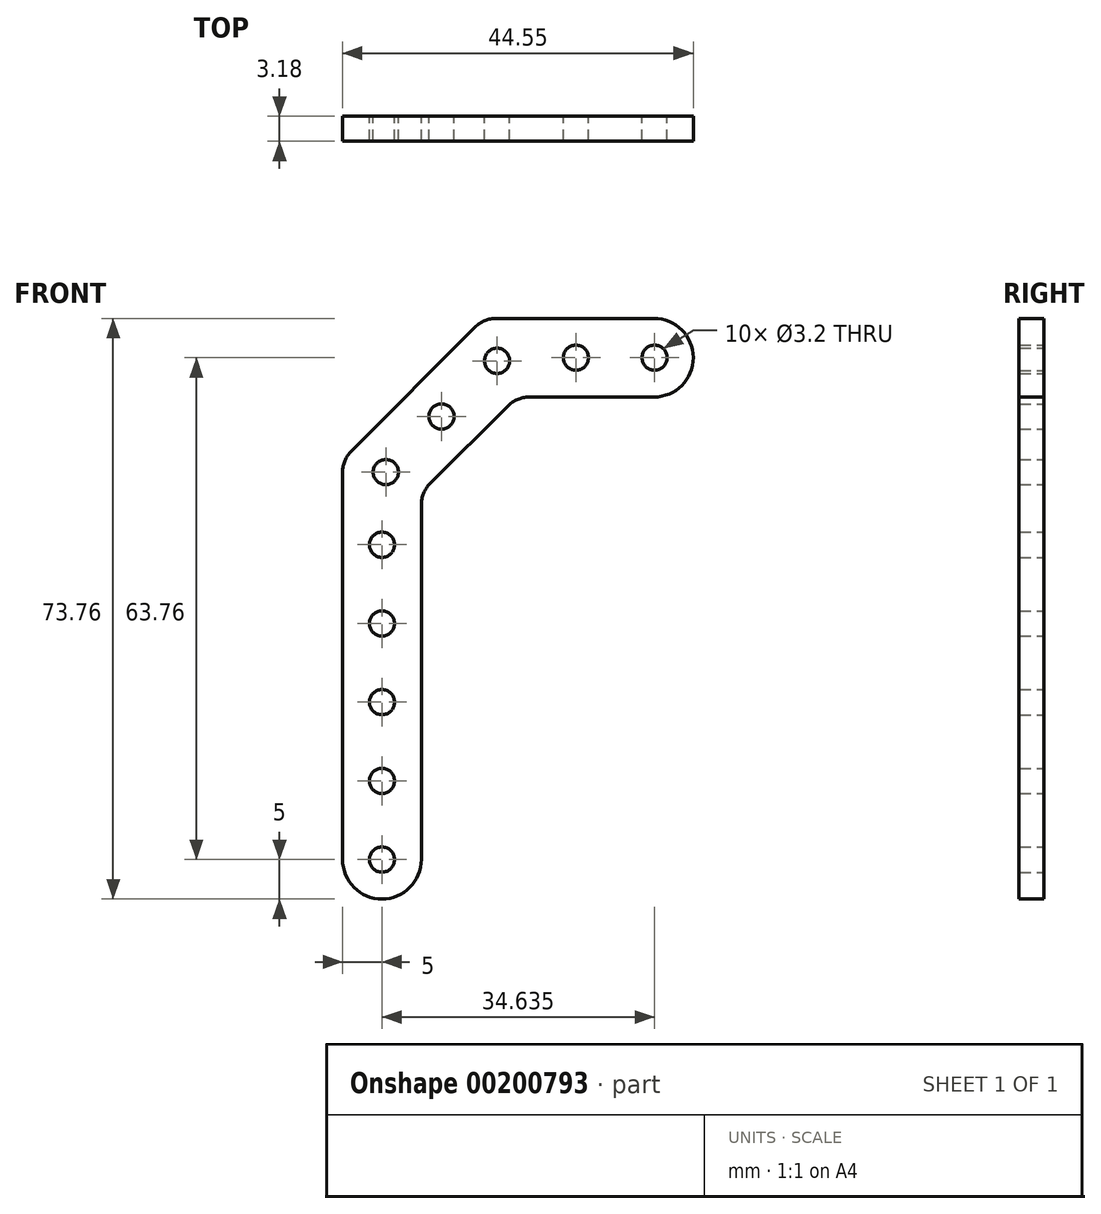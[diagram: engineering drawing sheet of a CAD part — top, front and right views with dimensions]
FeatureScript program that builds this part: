
annotation { "Feature Type Name" : "Feature", "Feature Type Description" : "" }
export const myFeature = defineFeature(function(context is Context, id is Id, definition is map)
    precondition{}
    {
        {
            var Q0;
            Q0=qCreatedBy(makeId("Front.planeOp"),FACE);
            var sketch = newSketch(context, id + "F0", { "sketchPlane" : qUnion([Q0])});
            skLineSegment(sketch, "E0", {"start": v(0, -68.76) * mm, "end": v(0, -19.54) * mm});
            skLineSegment(sketch, "E1", {"start": v(1.12, -16.84) * mm, "end": v(16.84, -1.12) * mm});
            skLineSegment(sketch, "E2", {"start": v(19.54, 0) * mm, "end": v(39.55, 0) * mm});
            skLineSegment(sketch, "E3.0", {"start": v(23.68, -10) * mm, "end": v(39.55, -10) * mm});
            skLineSegment(sketch, "E3.1", {"start": v(11.12, -20.99) * mm, "end": v(20.99, -11.12) * mm});
            skLineSegment(sketch, "E3.2", {"start": v(10, -68.76) * mm, "end": v(10, -23.68) * mm});
            skArc(sketch, "E4", {"start": v(0, -68.76) * mm, "mid": v(5, -73.76) * mm, "end": v(10, -68.76) * mm});
            skArc(sketch, "E5", {"start": v(39.55, -10) * mm, "mid": v(44.55, -5) * mm, "end": v(39.55, 0) * mm});
            skCircle(sketch, "E6", {"center": v(5, -68.76) * mm, "radius": 1.6 * mm});
            skCircle(sketch, "E7.0.1.0", {"center": v(5, -58.76) * mm, "radius": 1.6 * mm});
            skCircle(sketch, "E7.0.2.0", {"center": v(5, -48.76) * mm, "radius": 1.6 * mm});
            skCircle(sketch, "E7.0.3.0", {"center": v(5, -38.76) * mm, "radius": 1.6 * mm});
            skCircle(sketch, "E7.0.4.0", {"center": v(5, -28.76) * mm, "radius": 1.6 * mm});
            skLineSegment(sketch, "E7.direction1", {"start": v(5, -68.76) * mm, "end": v(29.21, -68.76) * mm, "construction": true});
            skLineSegment(sketch, "E7.direction2", {"start": v(5, -68.76) * mm, "end": v(5, -58.76) * mm, "construction": true});
            skPoint(sketch, "E8.visualSharp", {"position": v(0, -17.96) * mm});
            skArc(sketch, "E8.filletArc", {"start": v(1.12, -16.84) * mm, "mid": v(0.3, -18.08) * mm, "end": v(0, -19.54) * mm});
            skPoint(sketch, "E9.visualSharp", {"position": v(10, -22.1) * mm});
            skArc(sketch, "E9.filletArc", {"start": v(11.12, -20.99) * mm, "mid": v(10.3, -22.22) * mm, "end": v(10, -23.68) * mm});
            skPoint(sketch, "E10.visualSharp", {"position": v(22.1, -10) * mm});
            skArc(sketch, "E10.filletArc", {"start": v(23.68, -10) * mm, "mid": v(22.22, -10.3) * mm, "end": v(20.99, -11.12) * mm});
            skPoint(sketch, "E11.visualSharp", {"position": v(17.96, 0) * mm});
            skArc(sketch, "E11.filletArc", {"start": v(19.54, 0) * mm, "mid": v(18.08, -0.3) * mm, "end": v(16.84, -1.12) * mm});
            skCircle(sketch, "E12", {"center": v(5.5, -19.54) * mm, "radius": 1.6 * mm});
            skCircle(sketch, "E13", {"center": v(12.56, -12.47) * mm, "radius": 1.6 * mm});
            skCircle(sketch, "E14", {"center": v(19.64, -5.4) * mm, "radius": 1.6 * mm});
            skCircle(sketch, "E15", {"center": v(29.64, -5) * mm, "radius": 1.6 * mm});
            skCircle(sketch, "E16", {"center": v(39.64, -5) * mm, "radius": 1.6 * mm});
            skPoint(sketch, "E16.centerSnap0", {"position": v(44.55, -5) * mm});
            skSolve(sketch);
        }
        {
            var Q0;
            Q0=makeQuery(id+"F0.imprint","IMPRINT",FACE,{"disambiguationData":[TD([[makeQuery(id+"F0.imprint","IMPRINT",EDGE,{"derivedFrom":sQuery(id+"F0.wireOp",EDGE,"E0")}),-1.0]])]});
            extrude(context, id + "F1", {"entities" : qUnion([Q0]), "depth" : 3.17 * mm});
        }
    });
